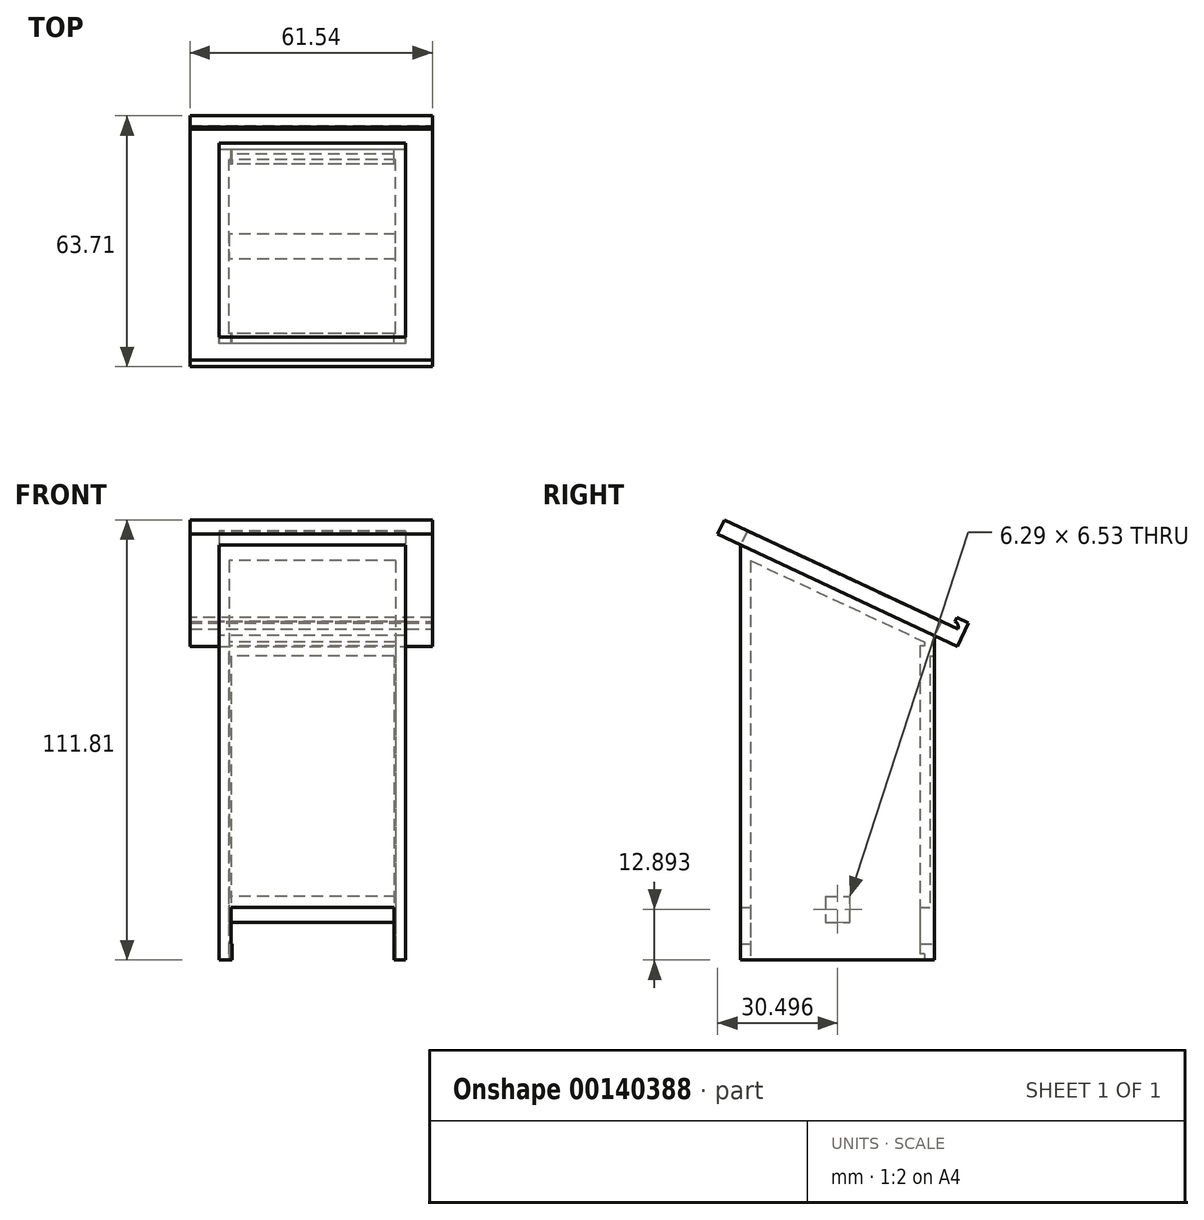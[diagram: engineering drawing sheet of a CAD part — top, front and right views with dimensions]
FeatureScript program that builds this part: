
annotation { "Feature Type Name" : "Feature", "Feature Type Description" : "" }
export const myFeature = defineFeature(function(context is Context, id is Id, definition is map)
    precondition{}
    {
        {
            var Q0;
            Q0=qCreatedBy(makeId("Right.planeOp"),FACE);
            var sketch = newSketch(context, id + "F0", { "sketchPlane" : qUnion([Q0])});
            skLineSegment(sketch, "E0.bottom", {"start": v(-24.64, 52.73) * mm, "end": v(24.64, 52.73) * mm});
            skLineSegment(sketch, "E0.top", {"start": v(-24.64, -52.73) * mm, "end": v(24.64, -52.73) * mm});
            skLineSegment(sketch, "E0.left", {"start": v(-24.64, 52.73) * mm, "end": v(-24.64, -52.73) * mm});
            skLineSegment(sketch, "E0.right", {"start": v(24.64, 52.73) * mm, "end": v(24.64, -52.73) * mm});
            skPoint(sketch, "E0.middle", {"position": v(0, 0) * mm});
            skLineSegment(sketch, "E1", {"start": v(-24.64, 52.73) * mm, "end": v(24.64, 29.7) * mm});
            skSolve(sketch);
        }
        {
            var Q0;
            {var subQ0=sQuery(id+"F0.wireOp",EDGE,"E0.top");Q0=makeQuery(id+"F0.imprint","IMPRINT",FACE,{"disambiguationData":[TD([[makeQuery(id+"F0.imprint","IMPRINT",EDGE,{"derivedFrom":subQ0}),1.0]])]});}
            extrude(context, id + "F1", {"entities" : qUnion([Q0]), "depth" : 47.43 * mm});
        }
        {
            var Q0;
            Q0=makeQuery(id+"F1.opExtrude","SWEPT_FACE",FACE,{"disambiguationData":[OSD([sQuery(id+"F0.wireOp",EDGE,"E1")])]});
            var sketch = newSketch(context, id + "F2", { "sketchPlane" : qUnion([Q0])});
            skLineSegment(sketch, "E2.bottom", {"start": v(-7.33, -51.1) * mm, "end": v(54.2, -51.1) * mm});
            skLineSegment(sketch, "E2.top", {"start": v(-7.33, 16.18) * mm, "end": v(54.2, 16.18) * mm});
            skLineSegment(sketch, "E2.left", {"start": v(-7.33, -51.1) * mm, "end": v(-7.33, 16.18) * mm});
            skLineSegment(sketch, "E2.right", {"start": v(54.2, -51.1) * mm, "end": v(54.2, 16.18) * mm});
            skPoint(sketch, "E2.middle", {"position": v(23.44, -17.46) * mm});
            skPoint(sketch, "E2.middle.positionSnap0", {"position": v(0, -17.46) * mm});
            skPoint(sketch, "E2.centerSnap0", {"position": v(0, -17.46) * mm});
            skSolve(sketch);
        }
        {
            var Q0;
            Q0=makeQuery(id+"F2.imprint","IMPRINT",FACE,{"disambiguationData":[TD([[makeQuery(id+"F2.imprint","IMPRINT",EDGE,{"derivedFrom":sQuery(id+"F2.wireOp",EDGE,"E2.bottom")}),1.0]])]});
            extrude(context, id + "F3", {"entities" : qUnion([Q0]), "depth" : 4 * mm});
        }
        {
            var Q0;
            Q0=makeQuery(id+"F1.opExtrude","SWEPT_FACE",FACE,{"disambiguationData":[OSD([sQuery(id+"F0.wireOp",EDGE,"E1")])]});
            extrude(context, id + "F4", {"entities" : qUnion([Q0]), "depth" : 3.8 * mm});
        }
        {
            var Q0;
            Q0=makeQuery(id+"F3.opExtrude","CAP_FACE",FACE,{"disambiguationData":[OSD([sQuery(id+"F0.wireOp",EDGE,"E0.bottom"),sQuery(id+"F0.wireOp",EDGE,"E0.left"),sQuery(id+"F0.wireOp",EDGE,"E0.right"),sQuery(id+"F0.wireOp",EDGE,"E1"),sQuery(id+"F2.wireOp",EDGE,"E2.bottom"),sQuery(id+"F2.wireOp",EDGE,"E2.top"),sQuery(id+"F2.wireOp",EDGE,"E2.left"),sQuery(id+"F2.wireOp",EDGE,"E2.right")])],"isStart":false});
            var sketch = newSketch(context, id + "F5", { "sketchPlane" : qUnion([Q0])});
            skLineSegment(sketch, "E3.bottom", {"start": v(54.2, 12.94) * mm, "end": v(-7.33, 12.94) * mm});
            skLineSegment(sketch, "E3.top", {"start": v(54.2, 16.18) * mm, "end": v(-7.33, 16.18) * mm});
            skLineSegment(sketch, "E3.left", {"start": v(54.2, 12.94) * mm, "end": v(54.2, 16.18) * mm});
            skLineSegment(sketch, "E3.right", {"start": v(-7.33, 12.94) * mm, "end": v(-7.33, 16.18) * mm});
            skSolve(sketch);
        }
        {
            var Q0;
            Q0=makeQuery(id+"F5.imprint","IMPRINT",FACE,{"disambiguationData":[TD([[makeQuery(id+"F5.imprint","IMPRINT",EDGE,{"derivedFrom":sQuery(id+"F5.wireOp",EDGE,"E3.bottom")}),-1.0]])]});
            extrude(context, id + "F6", {"entities" : qUnion([Q0]), "operationType" : NewBodyOperationType.ADD, "depth" : 2.55 * mm});
        }
        {
            var Q0;
            Q0=makeQuery(id+"F1.opExtrude","SWEPT_FACE",FACE,{"disambiguationData":[OSD([sQuery(id+"F0.wireOp",EDGE,"E0.right")])]});
            var sketch = newSketch(context, id + "F7", { "sketchPlane" : qUnion([Q0])});
            skLineSegment(sketch, "E4.bottom", {"start": v(-44.46, 24.6) * mm, "end": v(-3.08, 24.6) * mm});
            skLineSegment(sketch, "E4.top", {"start": v(-44.46, -48.64) * mm, "end": v(-3.08, -48.64) * mm});
            skLineSegment(sketch, "E4.left", {"start": v(-44.46, 24.6) * mm, "end": v(-44.46, -48.64) * mm});
            skLineSegment(sketch, "E4.right", {"start": v(-3.08, 24.6) * mm, "end": v(-3.08, -48.64) * mm});
            skSolve(sketch);
        }
        {
            var Q0;
            Q0=makeQuery(id+"F7.imprint","IMPRINT",FACE,{"disambiguationData":[TD([[makeQuery(id+"F7.imprint","IMPRINT",EDGE,{"derivedFrom":sQuery(id+"F7.wireOp",EDGE,"E4.bottom")}),-1.0]])]});
            extrude(context, id + "F8", {"entities" : qUnion([Q0]), "operationType" : NewBodyOperationType.REMOVE, "oppositeDirection" : true, "depth" : 1.16 * mm});
        }
        {
            var Q0;
            Q0=makeQuery(id+"F1.opExtrude","SWEPT_FACE",FACE,{"disambiguationData":[OSD([sQuery(id+"F0.wireOp",EDGE,"E0.top")])]});
            shell(context, id + "F9", {"entities" : qUnion([Q0]), "thickness" : 2.54 * mm});
        }
        {
            var Q0;
            Q0=makeQuery(id+"F8.boolean.opBoolean","COPY",FACE,{"derivedFrom":makeQuery(id+"F8.opExtrude","CAP_FACE",FACE,{"disambiguationData":[OSD([sQuery(id+"F7.wireOp",EDGE,"E4.bottom"),sQuery(id+"F7.wireOp",EDGE,"E4.top"),sQuery(id+"F7.wireOp",EDGE,"E4.left"),sQuery(id+"F7.wireOp",EDGE,"E4.right")])],"isStart":false})});
            var sketch = newSketch(context, id + "F10", { "sketchPlane" : qUnion([Q0])});
            skLineSegment(sketch, "E5.bottom", {"start": v(-44.46, -52.32) * mm, "end": v(-3.08, -52.32) * mm});
            skLineSegment(sketch, "E5.top", {"start": v(-44.46, -39.36) * mm, "end": v(-3.08, -39.36) * mm});
            skLineSegment(sketch, "E5.left", {"start": v(-44.46, -52.32) * mm, "end": v(-44.46, -39.36) * mm});
            skLineSegment(sketch, "E5.right", {"start": v(-3.08, -52.32) * mm, "end": v(-3.08, -39.36) * mm});
            skSolve(sketch);
        }
        {
            var Q0;
            {var subQ0=sQuery(id+"F10.wireOp",EDGE,"E5.top");Q0=makeQuery(id+"F10.imprint","IMPRINT",FACE,{"disambiguationData":[TD([[makeQuery(id+"F10.imprint","IMPRINT",EDGE,{"derivedFrom":subQ0}),-1.0]])]});}
            extrude(context, id + "F11", {"entities" : qUnion([Q0]), "operationType" : NewBodyOperationType.REMOVE, "oppositeDirection" : true, "depth" : 51.47 * mm});
        }
        {
            var Q0;
            Q0=makeQuery(id+"F1.opExtrude","SWEPT_FACE",FACE,{"disambiguationData":[OSD([sQuery(id+"F0.wireOp",EDGE,"E0.right")])]});
            var sketch = newSketch(context, id + "F12", { "sketchPlane" : qUnion([Q0])});
            skLineSegment(sketch, "E6.bottom", {"start": v(-44.46, -48.64) * mm, "end": v(-3.36, -48.64) * mm});
            skLineSegment(sketch, "E6.top", {"start": v(-44.46, -52.73) * mm, "end": v(-3.36, -52.73) * mm});
            skLineSegment(sketch, "E6.left", {"start": v(-44.46, -48.64) * mm, "end": v(-44.46, -52.73) * mm});
            skLineSegment(sketch, "E6.right", {"start": v(-3.36, -48.64) * mm, "end": v(-3.36, -52.73) * mm});
            skSolve(sketch);
        }
        {
            var Q0;
            Q0=makeQuery(id+"F12.imprint","IMPRINT",FACE,{"disambiguationData":[TD([[makeQuery(id+"F12.imprint","IMPRINT",EDGE,{"derivedFrom":sQuery(id+"F12.wireOp",EDGE,"E6.bottom")}),-1.0]])]});
            extrude(context, id + "F13", {"entities" : qUnion([Q0]), "operationType" : NewBodyOperationType.REMOVE, "oppositeDirection" : true, "depth" : 56.45 * mm});
        }
        {
            var Q0;
            {var subQ0=sQuery(id+"F0.wireOp",EDGE,"E1");var subQ1=sQuery(id+"F0.wireOp",EDGE,"E0.right");var subQ2=sQuery(id+"F0.wireOp",EDGE,"E0.left");var subQ3=sQuery(id+"F0.wireOp",EDGE,"E0.top");Q0=makeQuery(id+"F9.opShell","OFFSET_FACE",FACE,{"disambiguationData":[OSD([subQ3,subQ2,subQ1,subQ0]),TDD([makeQuery(id+"F1.opExtrude","CAP_FACE",FACE,{"disambiguationData":[OSD([subQ3,subQ2,subQ1,subQ0])],"isStart":true})])]});}
            var sketch = newSketch(context, id + "F14", { "sketchPlane" : qUnion([Q0])});
            skLineSegment(sketch, "E7.bottom", {"start": v(0, -43.1) * mm, "end": v(-3.12, -43.1) * mm});
            skLineSegment(sketch, "E7.top", {"start": v(0, -36.57) * mm, "end": v(-3.12, -36.57) * mm});
            skLineSegment(sketch, "E7.left", {"start": v(0, -43.1) * mm, "end": v(0, -36.57) * mm});
            skLineSegment(sketch, "E7.right", {"start": v(-3.12, -43.1) * mm, "end": v(-3.12, -36.57) * mm});
            skLineSegment(sketch, "E8.bottom", {"start": v(0, -43.1) * mm, "end": v(0, -43.1) * mm});
            skLineSegment(sketch, "E8.top", {"start": v(0, -36.57) * mm, "end": v(0, -36.57) * mm});
            skLineSegment(sketch, "E9.bottom", {"start": v(0, -36.57) * mm, "end": v(3.17, -36.57) * mm});
            skLineSegment(sketch, "E9.top", {"start": v(0, -43.1) * mm, "end": v(3.17, -43.1) * mm});
            skLineSegment(sketch, "E9.left", {"start": v(0, -36.57) * mm, "end": v(0, -43.1) * mm});
            skLineSegment(sketch, "E9.right", {"start": v(3.17, -36.57) * mm, "end": v(3.17, -43.1) * mm});
            skSolve(sketch);
        }
        {
            var Q0;
            Q0=makeQuery(id+"F14.imprint","IMPRINT",FACE,{"disambiguationData":[TD([[makeQuery(id+"F14.imprint","IMPRINT",EDGE,{"derivedFrom":sQuery(id+"F14.wireOp",EDGE,"E7.bottom")}),-1.0]])]});
            var Q1;
            Q1=makeQuery(id+"F14.imprint","IMPRINT",FACE,{"disambiguationData":[TD([[makeQuery(id+"F14.imprint","IMPRINT",EDGE,{"derivedFrom":sQuery(id+"F14.wireOp",EDGE,"E9.bottom")}),-1.0]])]});
            extrude(context, id + "F15", {"entities" : qUnion([Q0, Q1]), "operationType" : NewBodyOperationType.ADD, "depth" : 43.87 * mm});
        }
        {
            var Q0;
            Q0=makeQuery(id+"F1.opExtrude","SWEPT_FACE",FACE,{"disambiguationData":[OSD([sQuery(id+"F0.wireOp",EDGE,"E0.left")])]});
            var sketch = newSketch(context, id + "F16", { "sketchPlane" : qUnion([Q0])});
            skLineSegment(sketch, "E10.bottom", {"start": v(2.83, 45.56) * mm, "end": v(42.54, 45.56) * mm});
            skLineSegment(sketch, "E10.top", {"start": v(2.83, -35.69) * mm, "end": v(42.54, -35.69) * mm});
            skLineSegment(sketch, "E10.left", {"start": v(2.83, 45.56) * mm, "end": v(2.83, -35.69) * mm});
            skLineSegment(sketch, "E10.right", {"start": v(42.54, 45.56) * mm, "end": v(42.54, -35.69) * mm});
            skPoint(sketch, "E10.middle", {"position": v(22.68, 4.93) * mm});
            skSolve(sketch);
        }
        {
            var Q0;
            Q0=makeQuery(id+"F16.imprint","IMPRINT",FACE,{"disambiguationData":[TD([[makeQuery(id+"F16.imprint","IMPRINT",EDGE,{"derivedFrom":sQuery(id+"F16.wireOp",EDGE,"E10.bottom")}),-1.0]])]});
            extrude(context, id + "F17", {"entities" : qUnion([Q0]), "operationType" : NewBodyOperationType.REMOVE, "depth" : 10 * mm});
        }
        {
            var Q0;
            Q0=makeQuery(id+"F6.boolean.opBoolean","MERGE",FACE,{"derivedFrom":[makeQuery(id+"F3.opExtrude","SWEPT_FACE",FACE,{"disambiguationData":[OSD([sQuery(id+"F2.wireOp",EDGE,"E2.right")])]}),makeQuery(id+"F6.opExtrude","SWEPT_FACE",FACE,{"disambiguationData":[OSD([sQuery(id+"F5.wireOp",EDGE,"E3.left")])]})]});
            var sketch = newSketch(context, id + "F18", { "sketchPlane" : qUnion([Q0])});
            skCircle(sketch, "E11", {"center": v(29.22, 31.96) * mm, "radius": 1.45 * mm});
            skLineSegment(sketch, "E12", {"start": v(29.22, 31.96) * mm, "end": v(30.54, 31.34) * mm});
            skSolve(sketch);
        }
        {
            var Q0;
            {var subQ0=sQuery(id+"F18.wireOp",EDGE,"E12");Q0=makeQuery(id+"F18.imprint","IMPRINT",FACE,{"disambiguationData":[TD([[makeQuery(id+"F18.imprint","IMPRINT",EDGE,{"derivedFrom":subQ0}),1.0]])]});}
            extrude(context, id + "F19", {"entities" : qUnion([Q0]), "operationType" : NewBodyOperationType.REMOVE, "oppositeDirection" : true, "depth" : 80.75 * mm});
        }
    });
